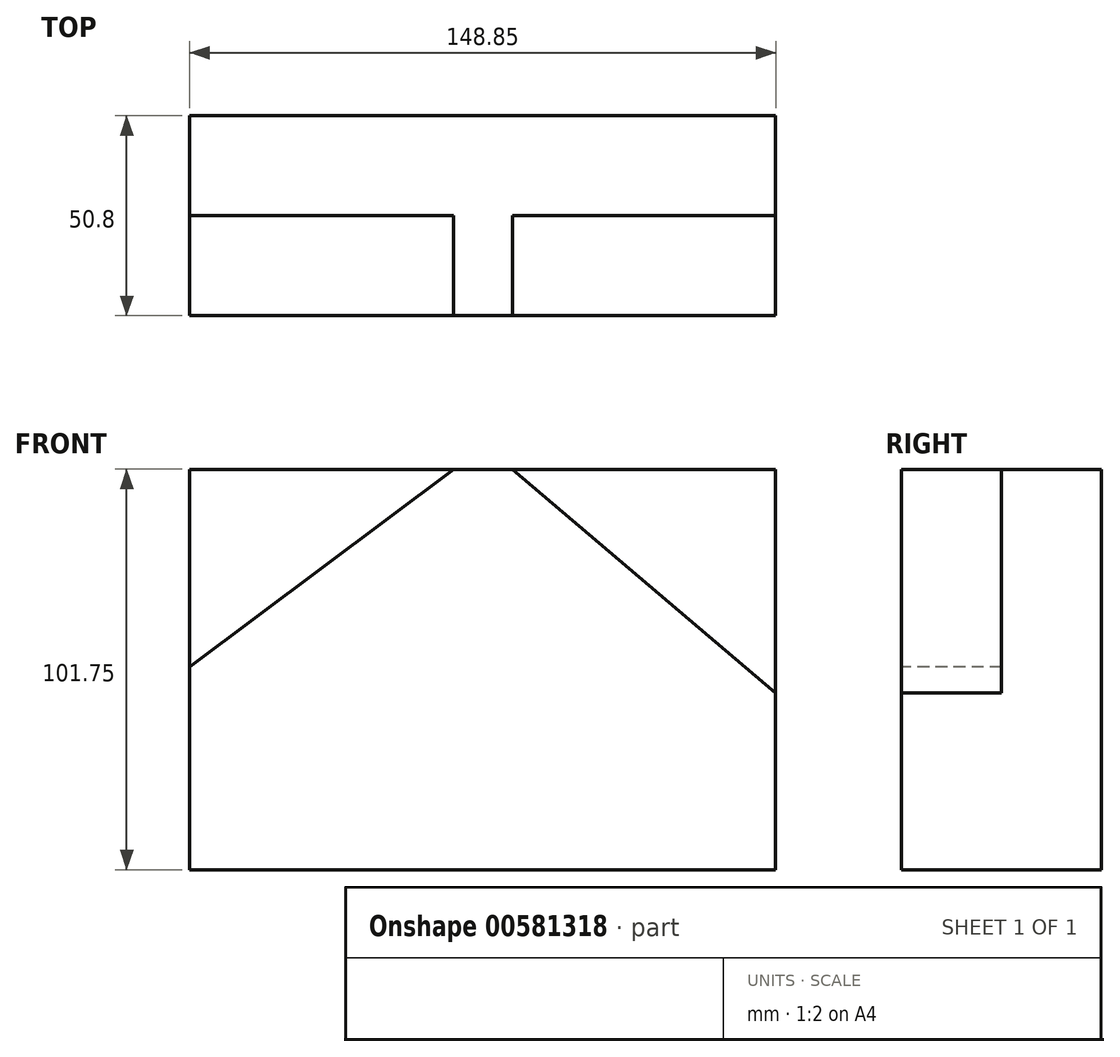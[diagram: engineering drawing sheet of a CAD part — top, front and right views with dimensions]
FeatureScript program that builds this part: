
annotation { "Feature Type Name" : "Feature", "Feature Type Description" : "" }
export const myFeature = defineFeature(function(context is Context, id is Id, definition is map)
    precondition{}
    {
        {
            var Q0;
            Q0=qCreatedBy(makeId("Front.planeOp"),FACE);
            var sketch = newSketch(context, id + "F0", { "sketchPlane" : qUnion([Q0])});
            skLineSegment(sketch, "E0.bottom", {"start": v(-76.12, 76.25) * mm, "end": v(72.73, 76.25) * mm});
            skLineSegment(sketch, "E0.top", {"start": v(-76.12, -25.5) * mm, "end": v(72.73, -25.5) * mm});
            skLineSegment(sketch, "E0.left", {"start": v(-76.12, 76.25) * mm, "end": v(-76.12, -25.5) * mm});
            skLineSegment(sketch, "E0.right", {"start": v(72.73, 76.25) * mm, "end": v(72.73, -25.5) * mm});
            skSolve(sketch);
        }
        {
            var Q0;
            Q0=makeQuery(id+"F0.imprint","IMPRINT",FACE,{"disambiguationData":[TD([[makeQuery(id+"F0.imprint","IMPRINT",EDGE,{"derivedFrom":sQuery(id+"F0.wireOp",EDGE,"E0.bottom")}),-1.0]])]});
            extrude(context, id + "F1", {"entities" : qUnion([Q0]), "depth" : 50.8 * mm, "offsetDistance" : 25.4 * mm});
        }
        {
            var Q0;
            Q0=makeQuery(id+"F1.opExtrude","CAP_FACE",FACE,{"disambiguationData":[OSD([sQuery(id+"F0.wireOp",EDGE,"E0.bottom"),sQuery(id+"F0.wireOp",EDGE,"E0.top"),sQuery(id+"F0.wireOp",EDGE,"E0.left"),sQuery(id+"F0.wireOp",EDGE,"E0.right")])],"isStart":false});
            var sketch = newSketch(context, id + "F2", { "sketchPlane" : qUnion([Q0])});
            skLineSegment(sketch, "E1.bottom", {"start": v(-76.12, 76.25) * mm, "end": v(72.73, 76.25) * mm});
            skLineSegment(sketch, "E1.top", {"start": v(-76.12, -25.5) * mm, "end": v(72.73, -25.5) * mm});
            skLineSegment(sketch, "E1.left", {"start": v(-76.12, 76.25) * mm, "end": v(-76.12, -25.5) * mm});
            skLineSegment(sketch, "E1.right", {"start": v(72.73, 76.25) * mm, "end": v(72.73, -25.5) * mm});
            skLineSegment(sketch, "E2", {"start": v(-9.08, 76.25) * mm, "end": v(-76.12, 26.01) * mm});
            skLineSegment(sketch, "E3", {"start": v(5.9, 76.25) * mm, "end": v(72.73, 19.37) * mm});
            skSolve(sketch);
        }
        {
            var Q0;
            Q0=makeQuery(id+"F2.imprint","IMPRINT",FACE,{"disambiguationData":[TD([[makeQuery(id+"F2.imprint","IMPRINT",EDGE,{"derivedFrom":sQuery(id+"F2.wireOp",EDGE,"E1.bottom")}),-1.0]])]});
            extrude(context, id + "F3", {"entities" : qUnion([Q0]), "operationType" : NewBodyOperationType.REMOVE, "oppositeDirection" : true, "depth" : 25.4 * mm, "offsetDistance" : 25.4 * mm});
        }
    });
